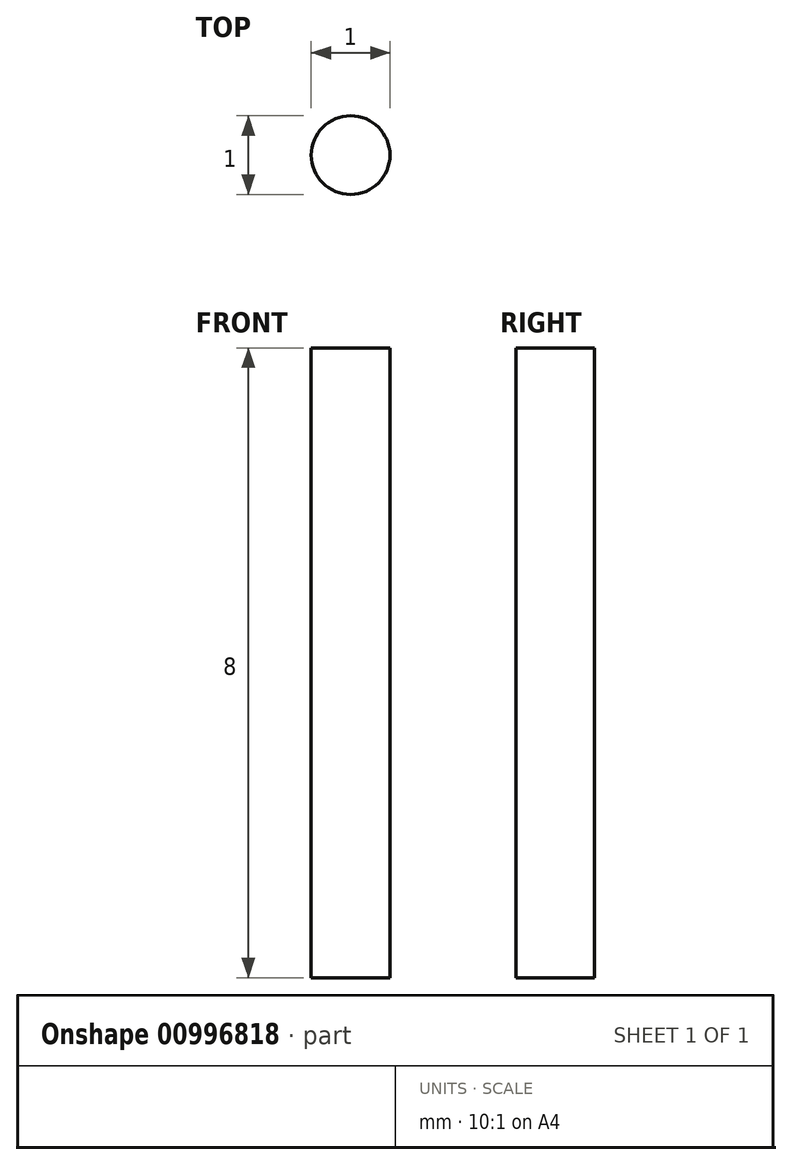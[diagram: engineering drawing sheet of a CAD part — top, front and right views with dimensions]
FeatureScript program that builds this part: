
annotation { "Feature Type Name" : "Feature", "Feature Type Description" : "" }
export const myFeature = defineFeature(function(context is Context, id is Id, definition is map)
    precondition{}
    {
        {
            var Q0;
            Q0=qCreatedBy(makeId("Top.planeOp"),FACE);
            var sketch = newSketch(context, id + "F0", { "sketchPlane" : qUnion([Q0])});
            skCircle(sketch, "E0", {"center": v(0, 0) * mm, "radius": 0.5 * mm});
            skSolve(sketch);
        }
        {
            var Q0;
            Q0 = qSketchRegion(id + "F0", true);
            extrude(context, id + "F1", {"entities" : qUnion([Q0]), "depth" : 8 * mm, "offsetDistance" : 25 * mm});
        }
    });
